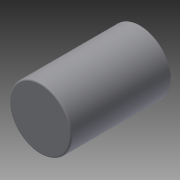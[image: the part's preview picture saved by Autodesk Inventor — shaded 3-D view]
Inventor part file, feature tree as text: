
AUTODESK INVENTOR PART (.ipt)
format: ipt  version: 2015 (Build 190159000, 159)  size: 98,816 bytes
history: native  units: mm
features: extrude x1, shell x1, fillet x1, sketch x1
ambient origin geometry x8: Origin, YZ Plane, XZ Plane, XY Plane, X Axis, Y Axis, Z Axis, Center Point
bodies: Solid1 (feature_tree)
feature tree (4):
  extrude  "Extrusion1"  Depth=125.0mm TaperAngle=0.0deg
  shell  "Shell1"  Thickness=5.0mm
  fillet  "Fillet1"  Radius=2.0mm
  sketch  "Sketch1"  dims[d0=77.5mm d1=125.0mm d2=0.0mm d3=5.0mm d5=2.0mm]
